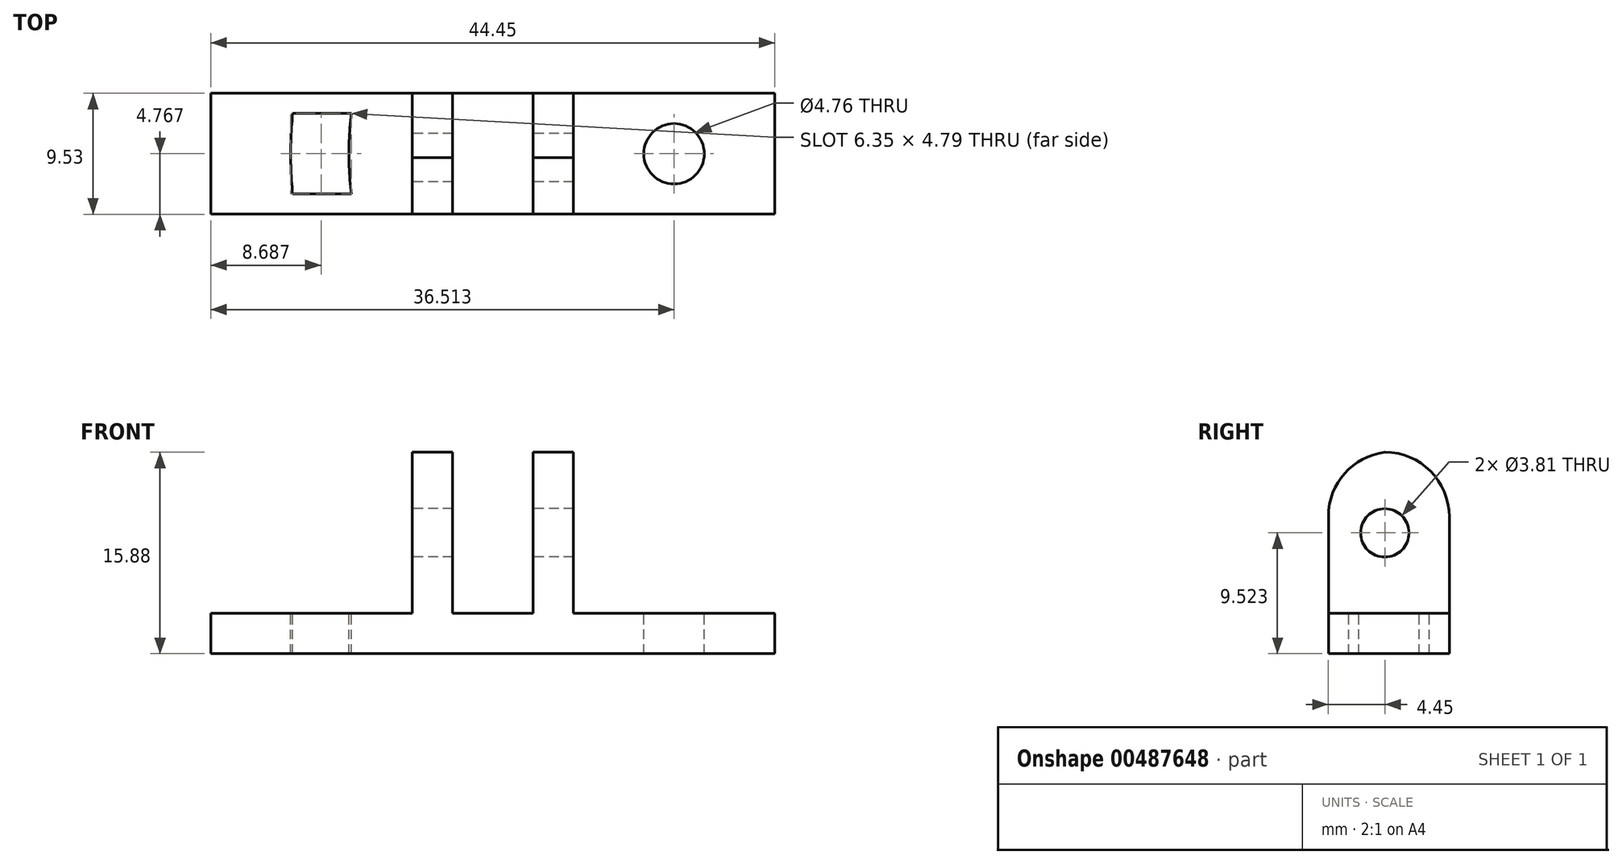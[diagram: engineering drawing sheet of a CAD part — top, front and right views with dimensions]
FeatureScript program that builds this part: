
annotation { "Feature Type Name" : "Feature", "Feature Type Description" : "" }
export const myFeature = defineFeature(function(context is Context, id is Id, definition is map)
    precondition{}
    {
        {
            var Q0;
            Q0=qCreatedBy(makeId("Front.planeOp"),FACE);
            var sketch = newSketch(context, id + "F0", { "sketchPlane" : qUnion([Q0])});
            skLineSegment(sketch, "E0.bottom", {"start": v(-3.18, 1.74) * mm, "end": v(0, 1.74) * mm});
            skLineSegment(sketch, "E0.left", {"start": v(-3.17, 1.74) * mm, "end": v(-3.17, -10.96) * mm});
            skLineSegment(sketch, "E0.right", {"start": v(0, 8.1) * mm, "end": v(0, -10.96) * mm});
            skLineSegment(sketch, "E1.bottom", {"start": v(-3.17, -10.96) * mm, "end": v(-19.05, -10.96) * mm});
            skLineSegment(sketch, "E1.top", {"start": v(0, -14.13) * mm, "end": v(-19.05, -14.13) * mm});
            skLineSegment(sketch, "E1.left", {"start": v(0, -14.12) * mm, "end": v(0, -14.13) * mm});
            skLineSegment(sketch, "E1.right", {"start": v(-19.05, -10.96) * mm, "end": v(-19.05, -14.13) * mm});
            skLineSegment(sketch, "E2.bottom", {"start": v(6.35, 1.75) * mm, "end": v(9.53, 1.75) * mm});
            skLineSegment(sketch, "E2.left", {"start": v(6.35, 1.75) * mm, "end": v(6.35, -10.95) * mm});
            skLineSegment(sketch, "E2.right", {"start": v(9.53, 1.75) * mm, "end": v(9.53, -10.95) * mm});
            skLineSegment(sketch, "E3.bottom", {"start": v(9.53, -10.95) * mm, "end": v(25.4, -10.95) * mm});
            skLineSegment(sketch, "E3.top", {"start": v(6.35, -14.12) * mm, "end": v(25.4, -14.12) * mm});
            skLineSegment(sketch, "E3.left", {"start": v(6.35, -10.95) * mm, "end": v(6.35, -10.96) * mm});
            skLineSegment(sketch, "E3.right", {"start": v(25.4, -10.95) * mm, "end": v(25.4, -14.12) * mm});
            skLineSegment(sketch, "E4.bottom", {"start": v(0, -10.96) * mm, "end": v(6.35, -10.96) * mm});
            skLineSegment(sketch, "E4.top", {"start": v(0, -14.12) * mm, "end": v(6.35, -14.12) * mm});
            skSolve(sketch);
        }
        {
            var Q0;
            Q0 = qSketchRegion(id + "F0", true);
            extrude(context, id + "F1", {"entities" : qUnion([Q0]), "depth" : 9.52 * mm, "offsetDistance" : 25.4 * mm});
        }
        {
            var Q0;
            Q0=makeQuery(id+"F1.opExtrude","CAP_EDGE",EDGE,{"disambiguationData":[OSD([sQuery(id+"F0.wireOp",EDGE,"E2.bottom")])],"isStart":true});
            var Q1;
            Q1=makeQuery(id+"F1.opExtrude","CAP_EDGE",EDGE,{"disambiguationData":[OSD([sQuery(id+"F0.wireOp",EDGE,"E0.bottom")])],"isStart":true});
            fillet(context, id + "F2", {"entities" : qUnion([Q0, Q1]), "radius" : 5.08 * mm, "tangentPropagation" : true, "allowEdgeOverflow" : false});
        }
        {
            var Q0;
            Q0=makeQuery(id+"F1.opExtrude","CAP_EDGE",EDGE,{"disambiguationData":[OSD([sQuery(id+"F0.wireOp",EDGE,"E2.bottom")])],"isStart":false});
            fillet(context, id + "F3", {"entities" : qUnion([Q0]), "radius" : 5.08 * mm, "tangentPropagation" : true, "allowEdgeOverflow" : false});
        }
        {
            var Q0;
            Q0=makeQuery(id+"F1.opExtrude","CAP_EDGE",EDGE,{"disambiguationData":[OSD([sQuery(id+"F0.wireOp",EDGE,"E0.bottom")])],"isStart":false});
            fillet(context, id + "F4", {"entities" : qUnion([Q0]), "radius" : 5.08 * mm, "tangentPropagation" : true, "allowEdgeOverflow" : false});
        }
        {
            var Q0;
            Q0=makeQuery(id+"F1.opExtrude","SWEPT_FACE",FACE,{"disambiguationData":[OSD([sQuery(id+"F0.wireOp",EDGE,"E0.left")])]});
            var sketch = newSketch(context, id + "F5", { "sketchPlane" : qUnion([Q0])});
            skLineSegment(sketch, "E5", {"start": v(5.08, 1.74) * mm, "end": v(5.08, -12.41) * mm, "construction": true});
            skLineSegment(sketch, "E6", {"start": v(5.08, -4.6) * mm, "end": v(14.14, -4.6) * mm, "construction": true});
            skLineSegment(sketch, "E7", {"start": v(5.08, 1.74) * mm, "end": v(14.54, 1.74) * mm, "construction": true});
            skCircle(sketch, "E8", {"center": v(5.08, -4.6) * mm, "radius": 1.9 * mm});
            skSolve(sketch);
        }
        {
            var Q0;
            Q0 = qSketchRegion(id + "F5", true);
            extrude(context, id + "F6", {"entities" : qUnion([Q0]), "operationType" : NewBodyOperationType.REMOVE, "endBound" : BoundingType.THROUGH_ALL, "oppositeDirection" : true, "depth" : 25.4 * mm, "offsetDistance" : 25.4 * mm});
        }
        {
            var Q0;
            Q0=makeQuery(id+"F1.opExtrude","SWEPT_FACE",FACE,{"disambiguationData":[OSD([sQuery(id+"F0.wireOp",EDGE,"E3.bottom")])]});
            var sketch = newSketch(context, id + "F7", { "sketchPlane" : qUnion([Q0])});
            skLineSegment(sketch, "E9", {"start": v(17.46, -9.53) * mm, "end": v(17.46, 0) * mm, "construction": true});
            skLineSegment(sketch, "E10", {"start": v(-10.56, -9.53) * mm, "end": v(-10.56, 0) * mm, "construction": true});
            skLineSegment(sketch, "E11", {"start": v(25.4, -4.76) * mm, "end": v(-19.37, -4.76) * mm, "construction": true});
            skCircle(sketch, "E12", {"center": v(17.46, -4.76) * mm, "radius": 2.38 * mm});
            skLineSegment(sketch, "E13.bottom", {"start": v(-7.97, -7.94) * mm, "end": v(-12.59, -7.94) * mm});
            skLineSegment(sketch, "E13.top", {"start": v(-7.97, -1.59) * mm, "end": v(-12.59, -1.59) * mm});
            skArc(sketch, "E14", {"start": v(-12.59, -1.59) * mm, "mid": v(-12.76, -4.76) * mm, "end": v(-12.59, -7.94) * mm});
            skArc(sketch, "E15", {"start": v(-7.97, -1.59) * mm, "mid": v(-8.17, -4.76) * mm, "end": v(-7.97, -7.94) * mm});
            skSolve(sketch);
        }
        {
            var Q0;
            Q0 = qSketchRegion(id + "F7", true);
            extrude(context, id + "F8", {"entities" : qUnion([Q0]), "operationType" : NewBodyOperationType.REMOVE, "endBound" : BoundingType.THROUGH_ALL, "oppositeDirection" : true, "depth" : 25.4 * mm, "offsetDistance" : 25.4 * mm});
        }
    });
